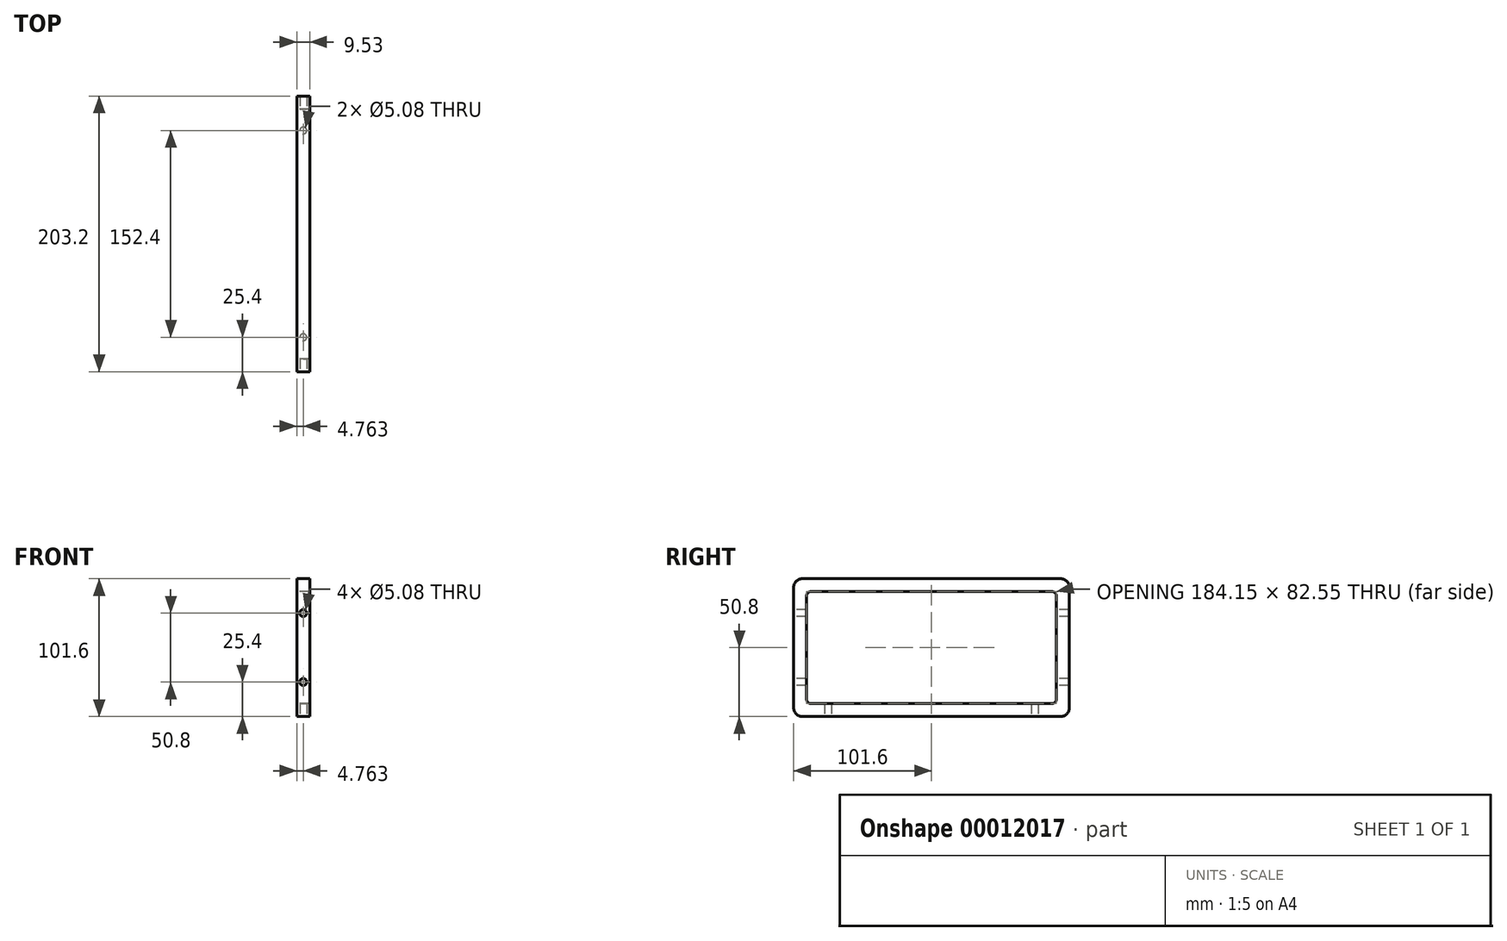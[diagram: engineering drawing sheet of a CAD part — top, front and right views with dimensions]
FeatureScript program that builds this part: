
annotation { "Feature Type Name" : "Feature", "Feature Type Description" : "" }
export const myFeature = defineFeature(function(context is Context, id is Id, definition is map)
    precondition{}
    {
        {
            var Q0;
            Q0=qCreatedBy(makeId("Right.planeOp"),FACE);
            var sketch = newSketch(context, id + "F0", { "sketchPlane" : qUnion([Q0])});
            skLineSegment(sketch, "E0.rect.bottom", {"start": v(95.25, 50.8) * mm, "end": v(-95.25, 50.8) * mm});
            skLineSegment(sketch, "E0.rect.top", {"start": v(95.25, -50.8) * mm, "end": v(-95.25, -50.8) * mm});
            skLineSegment(sketch, "E0.rect.left", {"start": v(101.6, 44.45) * mm, "end": v(101.6, -44.45) * mm});
            skLineSegment(sketch, "E0.rect.right", {"start": v(-101.6, 44.45) * mm, "end": v(-101.6, -44.45) * mm});
            skPoint(sketch, "E0.rect.middle", {"position": v(0, 0) * mm});
            skPoint(sketch, "E1.visualSharp", {"position": v(-101.6, 50.8) * mm});
            skArc(sketch, "E1.filletArc", {"start": v(-95.25, 50.8) * mm, "mid": v(-99.74, 48.94) * mm, "end": v(-101.6, 44.45) * mm});
            skPoint(sketch, "E2.visualSharp", {"position": v(-101.6, -50.8) * mm});
            skArc(sketch, "E2.filletArc", {"start": v(-101.6, -44.45) * mm, "mid": v(-99.74, -48.94) * mm, "end": v(-95.25, -50.8) * mm});
            skPoint(sketch, "E3.visualSharp", {"position": v(101.6, -50.8) * mm});
            skArc(sketch, "E3.filletArc", {"start": v(95.25, -50.8) * mm, "mid": v(99.74, -48.94) * mm, "end": v(101.6, -44.45) * mm});
            skPoint(sketch, "E4.visualSharp", {"position": v(101.6, 50.8) * mm});
            skArc(sketch, "E4.filletArc", {"start": v(101.6, 44.45) * mm, "mid": v(99.74, 48.94) * mm, "end": v(95.25, 50.8) * mm});
            skLineSegment(sketch, "E5.0", {"start": v(88.9, 41.28) * mm, "end": v(-88.9, 41.28) * mm});
            skLineSegment(sketch, "E5.1", {"start": v(92.08, 38.1) * mm, "end": v(92.08, -38.1) * mm});
            skLineSegment(sketch, "E5.2", {"start": v(88.9, -41.28) * mm, "end": v(-88.9, -41.28) * mm});
            skLineSegment(sketch, "E5.3", {"start": v(-92.08, 38.1) * mm, "end": v(-92.08, -38.1) * mm});
            skPoint(sketch, "E6.visualSharp", {"position": v(92.08, 41.28) * mm});
            skArc(sketch, "E6.filletArc", {"start": v(92.08, 38.1) * mm, "mid": v(91.15, 40.35) * mm, "end": v(88.9, 41.28) * mm});
            skPoint(sketch, "E7.visualSharp", {"position": v(92.08, -41.28) * mm});
            skArc(sketch, "E7.filletArc", {"start": v(88.9, -41.28) * mm, "mid": v(91.15, -40.35) * mm, "end": v(92.08, -38.1) * mm});
            skPoint(sketch, "E8.visualSharp", {"position": v(-92.08, -41.28) * mm});
            skArc(sketch, "E8.filletArc", {"start": v(-92.08, -38.1) * mm, "mid": v(-91.15, -40.35) * mm, "end": v(-88.9, -41.28) * mm});
            skPoint(sketch, "E9.visualSharp", {"position": v(-92.08, 41.28) * mm});
            skArc(sketch, "E9.filletArc", {"start": v(-88.9, 41.28) * mm, "mid": v(-91.15, 40.35) * mm, "end": v(-92.08, 38.1) * mm});
            skSolve(sketch);
        }
        {
            var Q0;
            Q0=makeQuery(id+"F0.imprint","IMPRINT",FACE,{"disambiguationData":[TD([[makeQuery(id+"F0.imprint","IMPRINT",EDGE,{"derivedFrom":sQuery(id+"F0.wireOp",EDGE,"E0.rect.bottom")}),1.0]])]});
            extrude(context, id + "F1", {"entities" : qUnion([Q0]), "depth" : 9.52 * mm});
        }
        {
            var Q0;
            Q0=makeQuery(id+"F1.opExtrude","SWEPT_FACE",FACE,{"disambiguationData":[OSD([sQuery(id+"F0.wireOp",EDGE,"E0.rect.right")])]});
            var sketch = newSketch(context, id + "F2", { "sketchPlane" : qUnion([Q0])});
            skLineSegment(sketch, "E10.0", {"start": v(9.53, 44.45) * mm, "end": v(0, 44.45) * mm});
            skPoint(sketch, "E11", {"position": v(4.76, 44.45) * mm});
            skCircle(sketch, "E12", {"center": v(4.76, 25.4) * mm, "radius": 2.54 * mm});
            skCircle(sketch, "E13", {"center": v(4.76, -25.4) * mm, "radius": 2.54 * mm});
            skSolve(sketch);
        }
        {
            var Q0;
            Q0=makeQuery(id+"F2.imprint","IMPRINT",FACE,{"disambiguationData":[TD([[makeQuery(id+"F2.imprint","IMPRINT",EDGE,{"derivedFrom":sQuery(id+"F2.wireOp",EDGE,"E12")}),1.0]])]});
            var Q1;
            Q1=makeQuery(id+"F2.imprint","IMPRINT",FACE,{"disambiguationData":[TD([[makeQuery(id+"F2.imprint","IMPRINT",EDGE,{"derivedFrom":sQuery(id+"F2.wireOp",EDGE,"E13")}),1.0]])]});
            extrude(context, id + "F3", {"entities" : qUnion([Q0, Q1]), "operationType" : NewBodyOperationType.REMOVE, "oppositeDirection" : true, "depth" : 254 * mm});
        }
        {
            var Q0;
            Q0=makeQuery(id+"F1.opExtrude","SWEPT_FACE",FACE,{"disambiguationData":[OSD([sQuery(id+"F0.wireOp",EDGE,"E0.rect.top")])]});
            var sketch = newSketch(context, id + "F4", { "sketchPlane" : qUnion([Q0])});
            skLineSegment(sketch, "E14.0", {"start": v(9.53, 95.25) * mm, "end": v(0, 95.25) * mm});
            skPoint(sketch, "E15", {"position": v(4.76, 95.25) * mm});
            skCircle(sketch, "E16", {"center": v(4.76, 76.2) * mm, "radius": 2.54 * mm});
            skCircle(sketch, "E17", {"center": v(4.76, -76.2) * mm, "radius": 2.54 * mm});
            skSolve(sketch);
        }
        {
            var Q0;
            Q0=makeQuery(id+"F4.imprint","IMPRINT",FACE,{"disambiguationData":[TD([[makeQuery(id+"F4.imprint","IMPRINT",EDGE,{"derivedFrom":sQuery(id+"F4.wireOp",EDGE,"E16")}),1.0]])]});
            var Q1;
            Q1=makeQuery(id+"F4.imprint","IMPRINT",FACE,{"disambiguationData":[TD([[makeQuery(id+"F4.imprint","IMPRINT",EDGE,{"derivedFrom":sQuery(id+"F4.wireOp",EDGE,"E17")}),1.0]])]});
            extrude(context, id + "F5", {"entities" : qUnion([Q0, Q1]), "operationType" : NewBodyOperationType.REMOVE, "oppositeDirection" : true, "depth" : 25.4 * mm});
        }
    });
